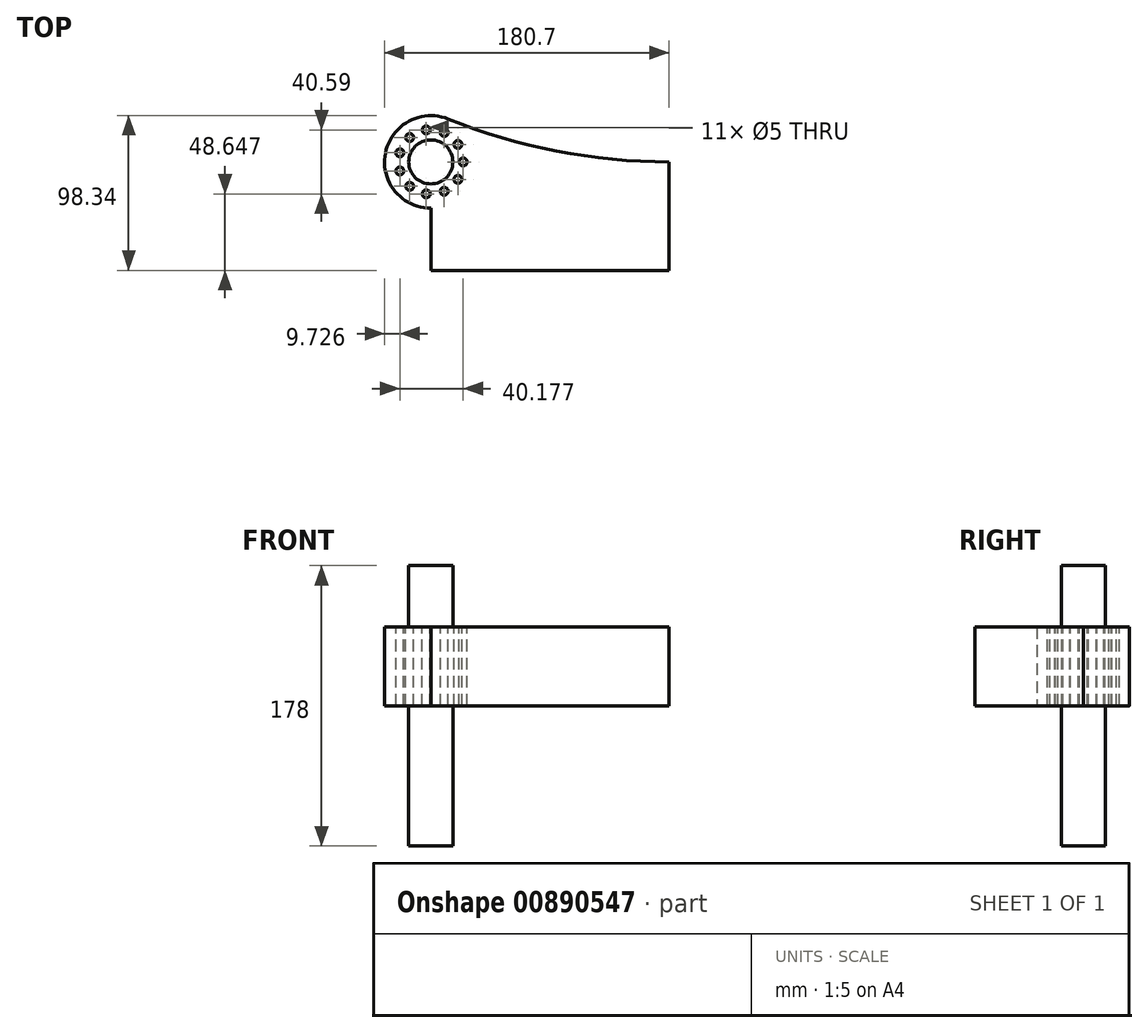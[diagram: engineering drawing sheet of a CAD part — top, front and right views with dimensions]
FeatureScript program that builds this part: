
annotation { "Feature Type Name" : "Feature", "Feature Type Description" : "" }
export const myFeature = defineFeature(function(context is Context, id is Id, definition is map)
    precondition{}
    {
        {
            var Q0;
            Q0=qCreatedBy(makeId("Top.planeOp"),FACE);
            var sketch = newSketch(context, id + "F0", { "sketchPlane" : qUnion([Q0])});
            skLineSegment(sketch, "E0.bottom", {"start": v(75.65, -34.47) * mm, "end": v(-75.65, -34.47) * mm});
            skLineSegment(sketch, "E0.top", {"start": v(75.65, 34.47) * mm, "end": v(-75.65, 34.47) * mm});
            skLineSegment(sketch, "E0.left", {"start": v(75.65, -34.47) * mm, "end": v(75.65, 34.47) * mm});
            skLineSegment(sketch, "E0.right", {"start": v(-75.65, -34.47) * mm, "end": v(-75.65, 34.47) * mm});
            skPoint(sketch, "E0.middle", {"position": v(0, 0) * mm});
            skCircle(sketch, "E1", {"center": v(-75.65, 34.47) * mm, "radius": 29.4 * mm});
            skArc(sketch, "E2", {"start": v(-64.64, 61.73) * mm, "mid": v(4.2, 41.35) * mm, "end": v(75.65, 34.47) * mm});
            skCircle(sketch, "E3", {"center": v(-75.65, 34.47) * mm, "radius": 14 * mm});
            skSolve(sketch);
        }
        {
            var Q0;
            {var subQ0=sQuery(id+"F0.wireOp",EDGE,"E1");var subQ2=sQuery(id+"F0.wireOp",EDGE,"E0.top");var subQ3=makeQuery(id+"F0.imprint","INTERSECT",VERTEX,{"derivedFrom":[subQ2,subQ0]});Q0=makeQuery(id+"F0.imprint","IMPRINT",FACE,{"disambiguationData":[TD([[makeQuery(id+"F0.imprint","IMPRINT",EDGE,{"disambiguationData":[TD([[subQ3,-1.0]])],"derivedFrom":subQ2}),-1.0]])]});}
            var Q1;
            {var subQ0=sQuery(id+"F0.wireOp",EDGE,"E2");Q1=makeQuery(id+"F0.imprint","IMPRINT",FACE,{"disambiguationData":[TD([[makeQuery(id+"F0.imprint","IMPRINT",EDGE,{"derivedFrom":subQ0}),-1.0]])]});}
            var Q2;
            {var subQ0=sQuery(id+"F0.wireOp",EDGE,"E1");var subQ1=sQuery(id+"F0.wireOp",EDGE,"E0.top");var subQ2=makeQuery(id+"F0.imprint","INTERSECT",VERTEX,{"derivedFrom":[subQ1,subQ0]});Q2=makeQuery(id+"F0.imprint","IMPRINT",FACE,{"disambiguationData":[TD([[makeQuery(id+"F0.imprint","IMPRINT",EDGE,{"disambiguationData":[TD([[subQ2,-1.0]])],"derivedFrom":subQ1}),1.0]])]});}
            var Q3;
            {var subQ5=sQuery(id+"F0.wireOp",EDGE,"E0.bottom");Q3=makeQuery(id+"F0.imprint","IMPRINT",FACE,{"disambiguationData":[TD([[makeQuery(id+"F0.imprint","IMPRINT",EDGE,{"derivedFrom":subQ5}),-1.0]])]});}
            extrude(context, id + "F1", {"entities" : qUnion([Q0, Q1, Q2, Q3]), "depth" : 25 * mm, "offsetDistance" : 25 * mm});
        }
        {
            var Q0;
            {var subQ0=sQuery(id+"F0.wireOp",EDGE,"E0.right");var subQ1=sQuery(id+"F0.wireOp",EDGE,"E0.top");var subQ2=makeQuery(id+"F0.imprint","INTERSECT",VERTEX,{"derivedFrom":[subQ1,subQ0]});Q0=makeQuery(id+"F0.imprint","IMPRINT",FACE,{"disambiguationData":[TD([[makeQuery(id+"F0.imprint","IMPRINT",EDGE,{"disambiguationData":[TD([[subQ2,1.0]])],"derivedFrom":subQ1}),-1.0]])]});}
            var Q1;
            {var subQ0=sQuery(id+"F0.wireOp",EDGE,"E0.right");var subQ1=sQuery(id+"F0.wireOp",EDGE,"E0.top");var subQ2=makeQuery(id+"F0.imprint","INTERSECT",VERTEX,{"derivedFrom":[subQ1,subQ0]});Q1=makeQuery(id+"F0.imprint","IMPRINT",FACE,{"disambiguationData":[TD([[makeQuery(id+"F0.imprint","IMPRINT",EDGE,{"disambiguationData":[TD([[subQ2,1.0]])],"derivedFrom":subQ1}),1.0]])]});}
            extrude(context, id + "F2", {"entities" : qUnion([Q0, Q1]), "operationType" : NewBodyOperationType.ADD, "endBound" : BoundingType.SYMMETRIC, "depth" : 178 * mm, "offsetDistance" : 25 * mm});
        }
        {
            var Q0;
            Q0=makeQuery(id+"F1.opExtrude","CAP_FACE",FACE,{"disambiguationData":[OSD([sQuery(id+"F0.wireOp",EDGE,"E0.bottom"),sQuery(id+"F0.wireOp",EDGE,"E0.left"),sQuery(id+"F0.wireOp",EDGE,"E0.right"),sQuery(id+"F0.wireOp",EDGE,"E1"),sQuery(id+"F0.wireOp",EDGE,"E2"),sQuery(id+"F0.wireOp",EDGE,"E3")])],"isStart":false});
            var sketch = newSketch(context, id + "F3", { "sketchPlane" : qUnion([Q0])});
            skPoint(sketch, "E4", {"position": v(-55.15, 34.47) * mm});
            skLineSegment(sketch, "E5.0", {"start": v(75.65, 34.47) * mm, "end": v(-75.65, 34.47) * mm, "construction": true});
            skPoint(sketch, "E6.1.0", {"position": v(-58.4, 45.56) * mm});
            skPoint(sketch, "E6.2.0", {"position": v(-67.13, 53.12) * mm});
            skPoint(sketch, "E6.3.0", {"position": v(-78.57, 54.77) * mm});
            skPoint(sketch, "E6.4.0", {"position": v(-89.08, 49.97) * mm});
            skPoint(sketch, "E6.5.0", {"position": v(-95.32, 40.25) * mm});
            skPoint(sketch, "E6.6.0", {"position": v(-95.32, 28.7) * mm});
            skPoint(sketch, "E6.7.0", {"position": v(-89.08, 18.98) * mm});
            skPoint(sketch, "E6.8.0", {"position": v(-78.57, 14.18) * mm});
            skPoint(sketch, "E6.9.0", {"position": v(-67.13, 15.82) * mm});
            skPoint(sketch, "E6.10.0", {"position": v(-58.4, 23.39) * mm});
            skPoint(sketch, "E6.center", {"position": v(-75.65, 34.47) * mm});
            skSolve(sketch);
        }
        {
            var Q0;
            Q0=sQuery(id+"F3.wireOp",VERTEX,"E6.3.0");
            var Q1;
            Q1=sQuery(id+"F3.wireOp",VERTEX,"E6.2.0");
            var Q2;
            Q2=sQuery(id+"F3.wireOp",VERTEX,"E6.1.0");
            var Q3;
            Q3=sQuery(id+"F3.wireOp",VERTEX,"E4");
            var Q4;
            Q4=sQuery(id+"F3.wireOp",VERTEX,"E6.10.0");
            var Q5;
            Q5=sQuery(id+"F3.wireOp",VERTEX,"E6.9.0");
            var Q6;
            Q6=sQuery(id+"F3.wireOp",VERTEX,"E6.8.0");
            var Q7;
            Q7=sQuery(id+"F3.wireOp",VERTEX,"E6.7.0");
            var Q8;
            Q8=sQuery(id+"F3.wireOp",VERTEX,"E6.6.0");
            var Q9;
            Q9=sQuery(id+"F3.wireOp",VERTEX,"E6.5.0");
            var Q10;
            Q10=sQuery(id+"F3.wireOp",VERTEX,"E6.4.0");
            var Q11;
            Q11=makeQuery(id+"F1.opExtrude","SWEPT_BODY",BODY,{"disambiguationData":[OSD([sQuery(id+"F0.wireOp",EDGE,"E0.bottom"),sQuery(id+"F0.wireOp",EDGE,"E0.left"),sQuery(id+"F0.wireOp",EDGE,"E0.right"),sQuery(id+"F0.wireOp",EDGE,"E1"),sQuery(id+"F0.wireOp",EDGE,"E2"),sQuery(id+"F0.wireOp",EDGE,"E3")])]});
            hole(context, id + "F4", {"style" : HoleStyle.SIMPLE, "endStyle" : HoleEndStyle.THROUGH, "holeDiameter" : 5 * mm, "majorDiameter" : 5 * mm, "isTappedThrough" : true, "tappedDepth" : 12 * mm, "tapClearance" : 3, "locations" : qUnion([Q0, Q1, Q2, Q3, Q4, Q5, Q6, Q7, Q8, Q9, Q10]), "scope" : qUnion([Q11])});
        }
        {
            var Q0;
            Q0=makeQuery(id+"F1.opExtrude","CAP_FACE",FACE,{"disambiguationData":[OSD([sQuery(id+"F0.wireOp",EDGE,"E0.bottom"),sQuery(id+"F0.wireOp",EDGE,"E0.left"),sQuery(id+"F0.wireOp",EDGE,"E0.right"),sQuery(id+"F0.wireOp",EDGE,"E1"),sQuery(id+"F0.wireOp",EDGE,"E2"),sQuery(id+"F0.wireOp",EDGE,"E3")])],"isStart":false});
            extrude(context, id + "F5", {"entities" : qUnion([Q0]), "operationType" : NewBodyOperationType.ADD, "depth" : 25 * mm, "offsetDistance" : 25 * mm});
        }
    });
